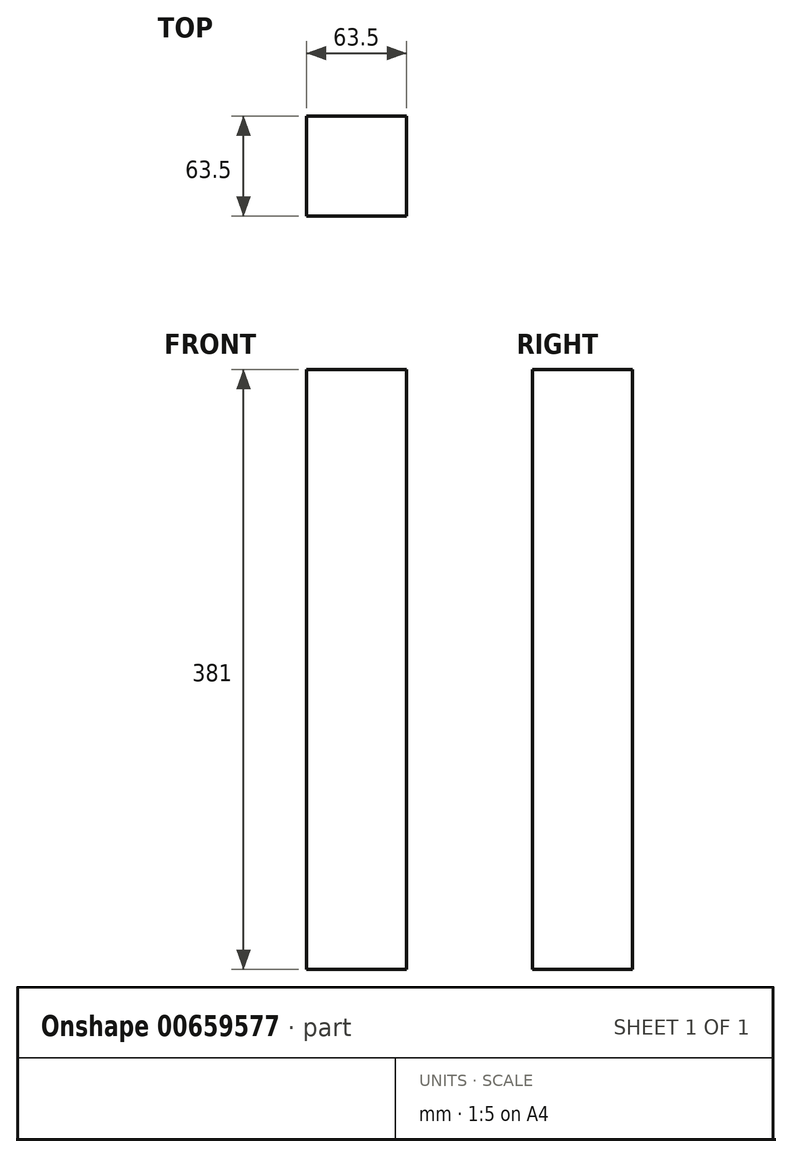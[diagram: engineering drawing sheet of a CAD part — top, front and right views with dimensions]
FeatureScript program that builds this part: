
annotation { "Feature Type Name" : "Feature", "Feature Type Description" : "" }
export const myFeature = defineFeature(function(context is Context, id is Id, definition is map)
    precondition{}
    {
        {
            var Q0;
            Q0=qCreatedBy(makeId("Top.planeOp"),FACE);
            var sketch = newSketch(context, id + "F0", { "sketchPlane" : qUnion([Q0])});
            skLineSegment(sketch, "E0.bottom", {"start": v(31.75, -31.75) * mm, "end": v(-31.75, -31.75) * mm});
            skLineSegment(sketch, "E0.top", {"start": v(31.75, 31.75) * mm, "end": v(-31.75, 31.75) * mm});
            skLineSegment(sketch, "E0.left", {"start": v(31.75, -31.75) * mm, "end": v(31.75, 31.75) * mm});
            skLineSegment(sketch, "E0.right", {"start": v(-31.75, -31.75) * mm, "end": v(-31.75, 31.75) * mm});
            skPoint(sketch, "E0.middle", {"position": v(0, 0) * mm});
            skSolve(sketch);
        }
        {
            var Q0;
            Q0=makeQuery(id+"F0.imprint","IMPRINT",FACE,{"disambiguationData":[TD([[makeQuery(id+"F0.imprint","IMPRINT",EDGE,{"derivedFrom":sQuery(id+"F0.wireOp",EDGE,"E0.bottom")}),-1.0]])]});
            extrude(context, id + "F1", {"entities" : qUnion([Q0]), "depth" : 381 * mm, "offsetDistance" : 25 * mm});
        }
    });
